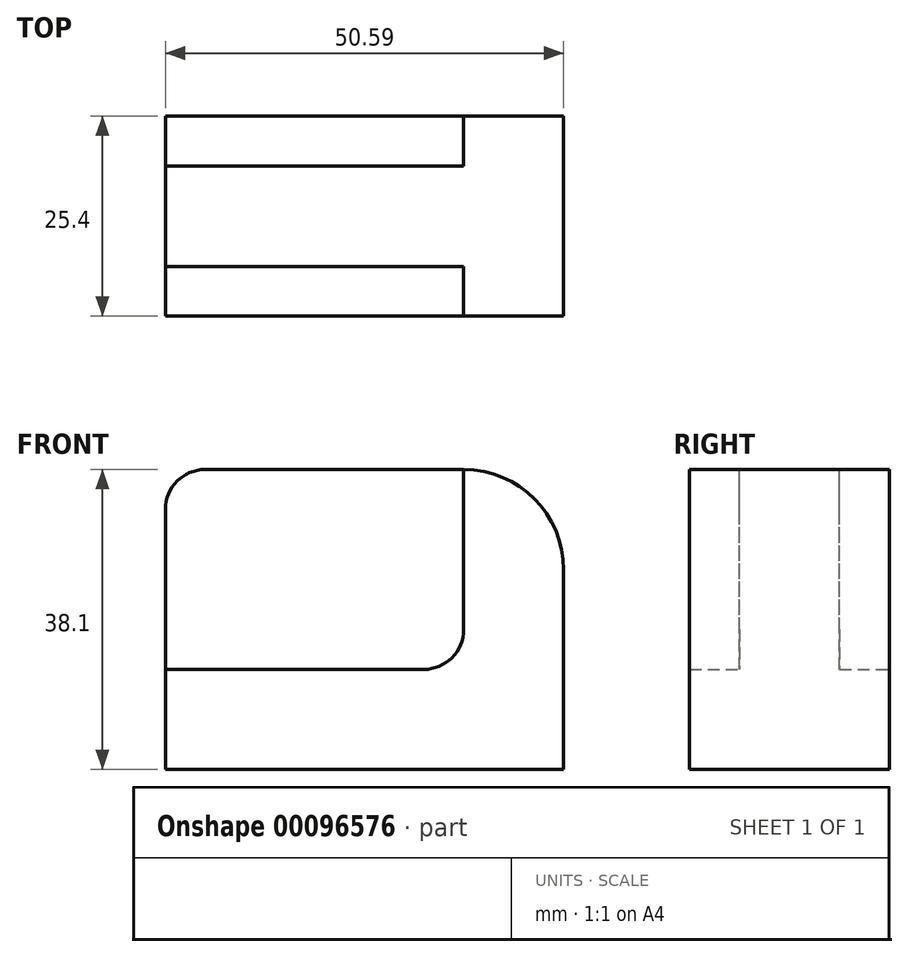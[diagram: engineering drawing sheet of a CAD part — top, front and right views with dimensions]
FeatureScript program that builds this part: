
annotation { "Feature Type Name" : "Feature", "Feature Type Description" : "" }
export const myFeature = defineFeature(function(context is Context, id is Id, definition is map)
    precondition{}
    {
        {
            var Q0;
            Q0=qCreatedBy(makeId("Front.planeOp"),FACE);
            var sketch = newSketch(context, id + "F0", { "sketchPlane" : qUnion([Q0])});
            skLineSegment(sketch, "E0", {"start": v(0, 0) * mm, "end": v(-50.6, 0) * mm});
            skLineSegment(sketch, "E1", {"start": v(-50.6, 0) * mm, "end": v(-50.6, 38.1) * mm});
            skLineSegment(sketch, "E2", {"start": v(-50.6, 38.1) * mm, "end": v(-12.7, 38.1) * mm});
            skLineSegment(sketch, "E3", {"start": v(0, 25.4) * mm, "end": v(0, 0) * mm});
            skPoint(sketch, "E4.visualSharp", {"position": v(0, 38.1) * mm});
            skArc(sketch, "E4.filletArc", {"start": v(0, 25.4) * mm, "mid": v(-3.72, 34.38) * mm, "end": v(-12.7, 38.1) * mm});
            skSolve(sketch);
        }
        {
            var Q0;
            Q0=makeQuery(id+"F0.imprint","IMPRINT",FACE,{"disambiguationData":[TD([[makeQuery(id+"F0.imprint","IMPRINT",EDGE,{"derivedFrom":sQuery(id+"F0.wireOp",EDGE,"E0")}),-1.0]])]});
            extrude(context, id + "F1", {"entities" : qUnion([Q0]), "depth" : 25.4 * mm});
        }
        {
            var Q0;
            Q0=makeQuery(id+"F1.opExtrude","SWEPT_FACE",FACE,{"disambiguationData":[OSD([sQuery(id+"F0.wireOp",EDGE,"E2")])]});
            var sketch = newSketch(context, id + "F2", { "sketchPlane" : qUnion([Q0])});
            skLineSegment(sketch, "E5", {"start": v(-12.7, 0) * mm, "end": v(-12.7, -6.35) * mm});
            skLineSegment(sketch, "E6", {"start": v(-12.7, -6.35) * mm, "end": v(-57.07, -6.35) * mm});
            skLineSegment(sketch, "E7", {"start": v(-57.07, -6.35) * mm, "end": v(-57.07, 0) * mm});
            skLineSegment(sketch, "E8", {"start": v(-57.07, 0) * mm, "end": v(-12.7, 0) * mm});
            skLineSegment(sketch, "E9", {"start": v(-12.7, -19.1) * mm, "end": v(-50.62, -19.1) * mm});
            skLineSegment(sketch, "E10", {"start": v(-50.62, -19.1) * mm, "end": v(-50.62, -25.45) * mm});
            skLineSegment(sketch, "E11", {"start": v(-50.62, -25.45) * mm, "end": v(-12.7, -25.45) * mm});
            skLineSegment(sketch, "E12", {"start": v(-12.7, -25.45) * mm, "end": v(-12.7, -19.1) * mm});
            skSolve(sketch);
        }
        {
            var Q0;
            {var subQ0=sQuery(id+"F2.wireOp",EDGE,"E5");Q0=makeQuery(id+"F2.imprint","IMPRINT",FACE,{"disambiguationData":[TD([[makeQuery(id+"F2.imprint","IMPRINT",EDGE,{"derivedFrom":subQ0}),1.0]])]});}
            var Q1;
            {var subQ2=sQuery(id+"F0.wireOp",EDGE,"E2");var subQ6=makeQuery(id+"F1.opExtrude","CAP_EDGE",EDGE,{"disambiguationData":[OSD([subQ2])],"isStart":false});Q1=makeQuery(id+"F2.imprint","IMPRINT",FACE,{"disambiguationData":[TD([[makeQuery(id+"F2.imprint","IMPRINT",EDGE,{"derivedFrom":subQ6}),1.0]])]});}
            extrude(context, id + "F3", {"entities" : qUnion([Q0, Q1]), "operationType" : NewBodyOperationType.REMOVE, "oppositeDirection" : true, "depth" : 25.4 * mm});
        }
        {
            var Q0;
            Q0=makeQuery(id+"F3.boolean.opBoolean","COPY",EDGE,{"derivedFrom":makeQuery(id+"F3.opExtrude","CAP_EDGE",EDGE,{"disambiguationData":[OSD([sQuery(id+"F2.wireOp",EDGE,"E12")])],"isStart":false})});
            var Q1;
            Q1=makeQuery(id+"F3.boolean.opBoolean","COPY",EDGE,{"derivedFrom":makeQuery(id+"F3.opExtrude","CAP_EDGE",EDGE,{"disambiguationData":[OSD([sQuery(id+"F2.wireOp",EDGE,"E5")])],"isStart":false})});
            var Q2;
            Q2=makeQuery(id+"F1.opExtrude","SWEPT_EDGE",EDGE,{"disambiguationData":[OSD([sQuery(id+"F0.wireOp",EDGE,"E1"),sQuery(id+"F0.wireOp",EDGE,"E2")])]});
            fillet(context, id + "F4", {"entities" : qUnion([Q0, Q1, Q2]), "radius" : 5.08 * mm, "tangentPropagation" : true, "allowEdgeOverflow" : false});
        }
    });
